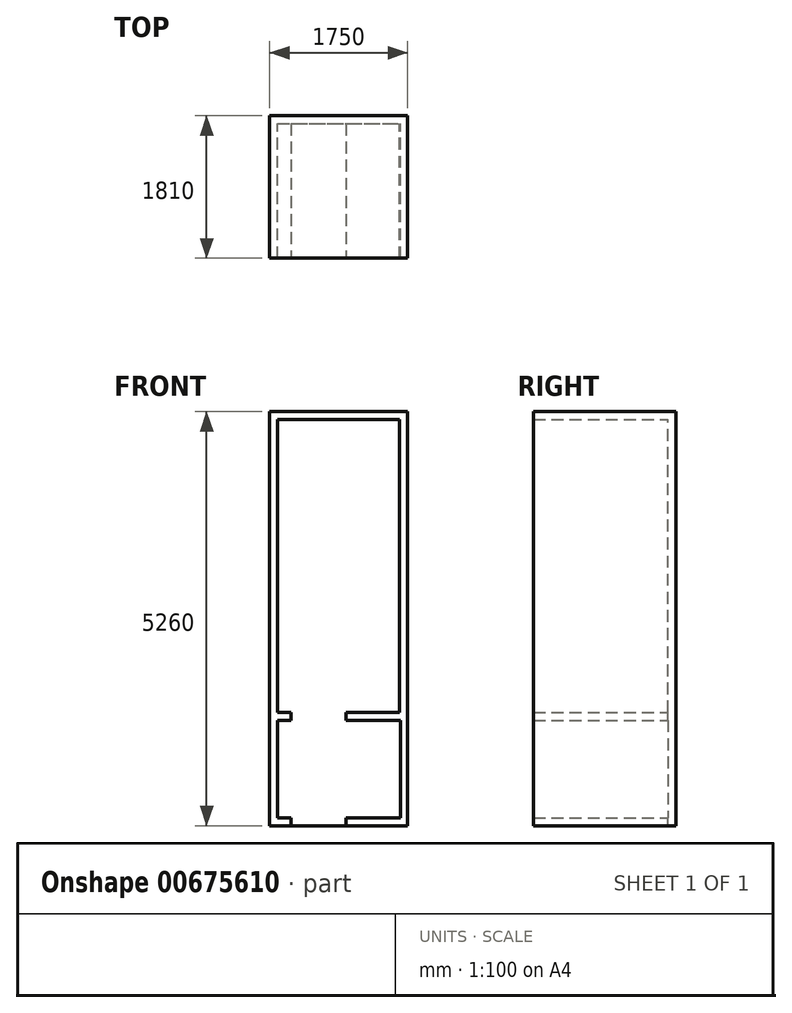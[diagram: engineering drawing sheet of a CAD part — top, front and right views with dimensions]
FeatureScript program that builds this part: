
annotation { "Feature Type Name" : "Feature", "Feature Type Description" : "" }
export const myFeature = defineFeature(function(context is Context, id is Id, definition is map)
    precondition{}
    {
        {
            var Q0;
            Q0=qCreatedBy(makeId("Front.planeOp"),FACE);
            var sketch = newSketch(context, id + "F0", { "sketchPlane" : qUnion([Q0])});
            skLineSegment(sketch, "E0.bottom", {"start": v(0, -644.38) * mm, "end": v(1550, -644.38) * mm});
            skLineSegment(sketch, "E0.top", {"start": v(0, 3075.62) * mm, "end": v(1550, 3075.62) * mm});
            skLineSegment(sketch, "E0.left", {"start": v(0, -644.38) * mm, "end": v(0, 3075.62) * mm});
            skLineSegment(sketch, "E0.right", {"start": v(1550, -644.38) * mm, "end": v(1550, 3075.62) * mm});
            skLineSegment(sketch, "E1.bottom", {"start": v(0, -744.38) * mm, "end": v(1558.93, -744.38) * mm});
            skLineSegment(sketch, "E1.top", {"start": v(0, -1984.38) * mm, "end": v(1558.93, -1984.38) * mm});
            skLineSegment(sketch, "E1.left", {"start": v(0, -744.38) * mm, "end": v(0, -1984.38) * mm});
            skLineSegment(sketch, "E1.right", {"start": v(1558.93, -744.38) * mm, "end": v(1558.93, -1984.38) * mm});
            skLineSegment(sketch, "E2.bottom", {"start": v(-100, 3175.62) * mm, "end": v(1650, 3175.62) * mm});
            skLineSegment(sketch, "E2.top", {"start": v(-100, -2084.38) * mm, "end": v(1650, -2084.38) * mm});
            skLineSegment(sketch, "E2.left", {"start": v(-100, 3175.62) * mm, "end": v(-100, -2084.38) * mm});
            skLineSegment(sketch, "E2.right", {"start": v(1650, 3175.62) * mm, "end": v(1650, -2084.38) * mm});
            skSolve(sketch);
        }
        {
            var Q0;
            Q0=makeQuery(id+"F0.imprint","IMPRINT",FACE,{"disambiguationData":[TD([[makeQuery(id+"F0.imprint","IMPRINT",EDGE,{"derivedFrom":sQuery(id+"F0.wireOp",EDGE,"E0.bottom")}),-1.0]])]});
            extrude(context, id + "F1", {"entities" : qUnion([Q0]), "depth" : 2700 * mm, "offsetDistance" : 25 * mm});
        }
        {
            var Q0;
            Q0=makeQuery(id+"F1.opExtrude","CAP_FACE",FACE,{"disambiguationData":[OSD([sQuery(id+"F0.wireOp",EDGE,"E0.bottom"),sQuery(id+"F0.wireOp",EDGE,"E0.top"),sQuery(id+"F0.wireOp",EDGE,"E0.left"),sQuery(id+"F0.wireOp",EDGE,"E0.right"),sQuery(id+"F0.wireOp",EDGE,"E1.bottom"),sQuery(id+"F0.wireOp",EDGE,"E1.top"),sQuery(id+"F0.wireOp",EDGE,"E1.left"),sQuery(id+"F0.wireOp",EDGE,"E1.right"),sQuery(id+"F0.wireOp",EDGE,"E2.bottom"),sQuery(id+"F0.wireOp",EDGE,"E2.top"),sQuery(id+"F0.wireOp",EDGE,"E2.left"),sQuery(id+"F0.wireOp",EDGE,"E2.right")])],"isStart":true});
            var sketch = newSketch(context, id + "F2", { "sketchPlane" : qUnion([Q0])});
            skLineSegment(sketch, "E3.bottom", {"start": v(100, 3175.62) * mm, "end": v(-1650, 3175.62) * mm});
            skLineSegment(sketch, "E3.top", {"start": v(100, -2084.38) * mm, "end": v(-1650, -2084.38) * mm});
            skLineSegment(sketch, "E3.left", {"start": v(100, 3175.62) * mm, "end": v(100, -2084.38) * mm});
            skLineSegment(sketch, "E3.right", {"start": v(-1650, 3175.62) * mm, "end": v(-1650, -2084.38) * mm});
            skSolve(sketch);
        }
        {
            var Q0;
            Q0 = qSketchRegion(id + "F2", true);
            extrude(context, id + "F3", {"entities" : qUnion([Q0]), "operationType" : NewBodyOperationType.ADD, "depth" : 100 * mm, "offsetDistance" : 25 * mm});
        }
        {
            var Q0;
            Q0=makeQuery(id+"F1.opExtrude","SWEPT_FACE",FACE,{"disambiguationData":[OSD([sQuery(id+"F0.wireOp",EDGE,"E0.bottom")])]});
            var sketch = newSketch(context, id + "F4", { "sketchPlane" : qUnion([Q0])});
            skLineSegment(sketch, "E4.bottom", {"start": v(170, 0) * mm, "end": v(870, 0) * mm});
            skLineSegment(sketch, "E4.top", {"start": v(170, -2200) * mm, "end": v(870, -2200) * mm});
            skLineSegment(sketch, "E4.left", {"start": v(170, 0) * mm, "end": v(170, -2200) * mm});
            skLineSegment(sketch, "E4.right", {"start": v(870, 0) * mm, "end": v(870, -2200) * mm});
            skSolve(sketch);
        }
        {
            var Q0;
            Q0 = qSketchRegion(id + "F4", true);
            extrude(context, id + "F5", {"entities" : qUnion([Q0]), "operationType" : NewBodyOperationType.REMOVE, "oppositeDirection" : true, "depth" : 3089.34 * mm, "offsetDistance" : 25 * mm});
        }
        {
            var Q0;
            Q0=makeQuery(id+"F1.opExtrude","CAP_FACE",FACE,{"disambiguationData":[OSD([sQuery(id+"F0.wireOp",EDGE,"E0.bottom"),sQuery(id+"F0.wireOp",EDGE,"E0.top"),sQuery(id+"F0.wireOp",EDGE,"E0.left"),sQuery(id+"F0.wireOp",EDGE,"E0.right"),sQuery(id+"F0.wireOp",EDGE,"E1.bottom"),sQuery(id+"F0.wireOp",EDGE,"E1.top"),sQuery(id+"F0.wireOp",EDGE,"E1.left"),sQuery(id+"F0.wireOp",EDGE,"E1.right"),sQuery(id+"F0.wireOp",EDGE,"E2.bottom"),sQuery(id+"F0.wireOp",EDGE,"E2.top"),sQuery(id+"F0.wireOp",EDGE,"E2.left"),sQuery(id+"F0.wireOp",EDGE,"E2.right")])],"isStart":false});
            var sketch = newSketch(context, id + "F6", { "sketchPlane" : qUnion([Q0])});
            skLineSegment(sketch, "E5.bottom", {"start": v(-1049.94, 4134.73) * mm, "end": v(2572.2, 4134.73) * mm});
            skLineSegment(sketch, "E5.top", {"start": v(-1049.94, -3144.76) * mm, "end": v(2572.2, -3144.76) * mm});
            skLineSegment(sketch, "E5.left", {"start": v(-1049.94, 4134.73) * mm, "end": v(-1049.94, -3144.76) * mm});
            skLineSegment(sketch, "E5.right", {"start": v(2572.2, 4134.73) * mm, "end": v(2572.2, -3144.76) * mm});
            skSolve(sketch);
        }
        {
            var Q0;
            Q0=makeQuery(id+"F6.imprint","IMPRINT",FACE,{"disambiguationData":[TD([[makeQuery(id+"F6.imprint","IMPRINT",EDGE,{"derivedFrom":sQuery(id+"F6.wireOp",EDGE,"E5.bottom")}),-1.0]])]});
            var Q1;
            Q1=makeQuery(id+"F6.imprint","IMPRINT",FACE,{"disambiguationData":[TD([[makeQuery(id+"F6.imprint","IMPRINT",EDGE,{"derivedFrom":makeQuery(id+"F1.opExtrude","CAP_EDGE",EDGE,{"disambiguationData":[OSD([sQuery(id+"F0.wireOp",EDGE,"E0.bottom")])],"isStart":false})}),1.0]])]});
            var Q2;
            Q2=makeQuery(id+"F6.imprint","IMPRINT",FACE,{"disambiguationData":[TD([[makeQuery(id+"F6.imprint","IMPRINT",EDGE,{"derivedFrom":makeQuery(id+"F1.opExtrude","CAP_EDGE",EDGE,{"disambiguationData":[OSD([sQuery(id+"F0.wireOp",EDGE,"E0.bottom")])],"isStart":false})}),-1.0]])]});
            var Q3;
            Q3=makeQuery(id+"F6.imprint","IMPRINT",FACE,{"disambiguationData":[TD([[makeQuery(id+"F6.imprint","IMPRINT",EDGE,{"derivedFrom":makeQuery(id+"F1.opExtrude","CAP_EDGE",EDGE,{"disambiguationData":[OSD([sQuery(id+"F0.wireOp",EDGE,"E1.bottom")])],"isStart":false})}),-1.0]])]});
            extrude(context, id + "F7", {"entities" : qUnion([Q0, Q1, Q2, Q3]), "operationType" : NewBodyOperationType.REMOVE, "oppositeDirection" : true, "depth" : 990 * mm, "offsetDistance" : 25 * mm});
        }
    });
